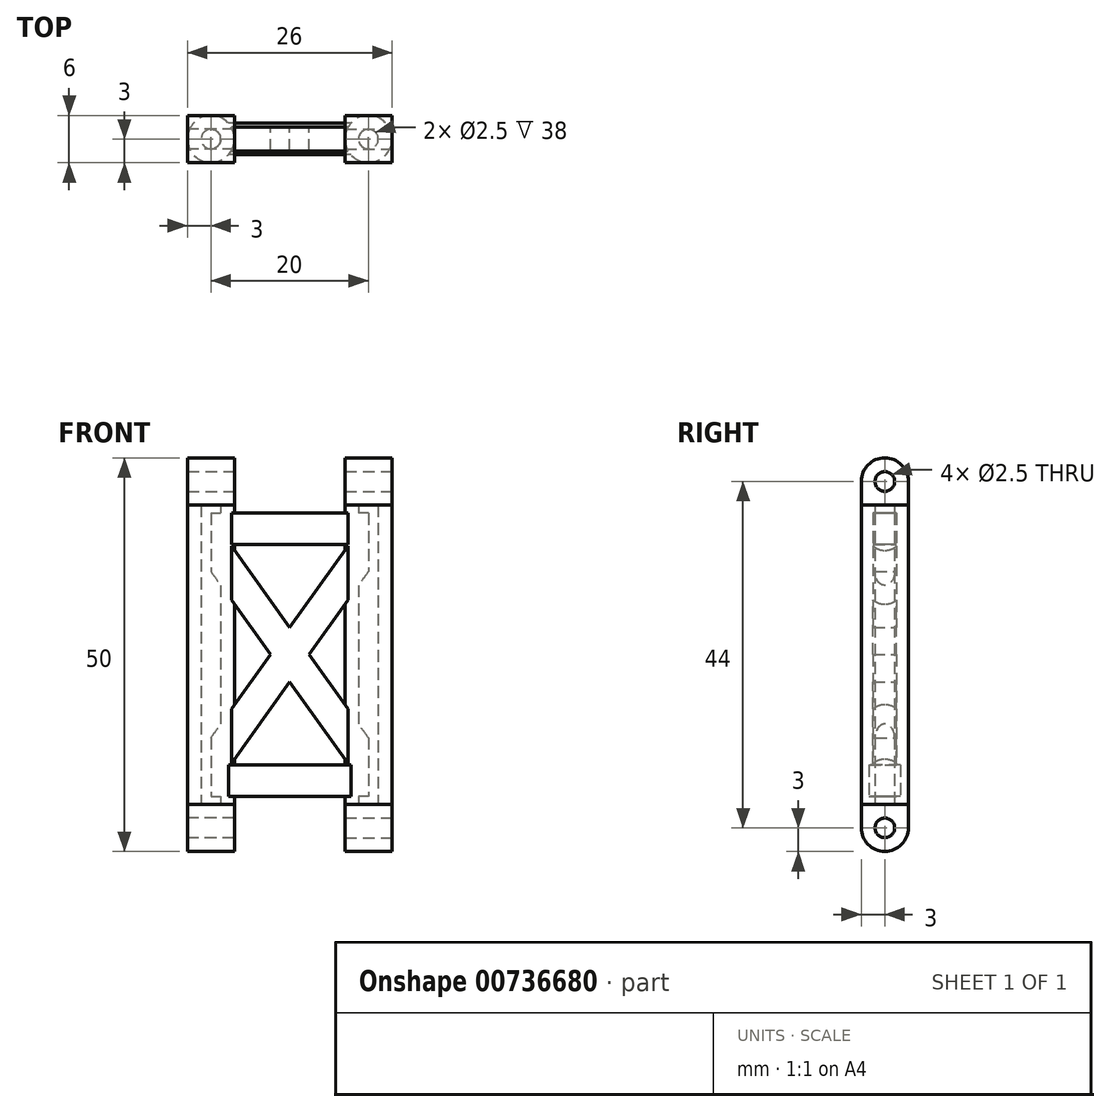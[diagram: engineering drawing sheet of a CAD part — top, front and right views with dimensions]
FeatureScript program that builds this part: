
annotation { "Feature Type Name" : "Feature", "Feature Type Description" : "" }
export const myFeature = defineFeature(function(context is Context, id is Id, definition is map)
    precondition{}
    {
        {
            var Q0;
            Q0=qCreatedBy(makeId("Top.planeOp"),FACE);
            var sketch = newSketch(context, id + "F0", { "sketchPlane" : qUnion([Q0])});
            skCircle(sketch, "E0", {"center": v(-10, 0) * mm, "radius": 3 * mm});
            skCircle(sketch, "E1", {"center": v(10, 0) * mm, "radius": 3 * mm});
            skCircle(sketch, "E2", {"center": v(-10, 0) * mm, "radius": 1.25 * mm});
            skCircle(sketch, "E3", {"center": v(10, 0) * mm, "radius": 1.25 * mm});
            skLineSegment(sketch, "E4.bottom", {"start": v(-13, 3) * mm, "end": v(-7, 3) * mm});
            skLineSegment(sketch, "E4.top", {"start": v(-13, -3) * mm, "end": v(-7, -3) * mm});
            skLineSegment(sketch, "E4.left", {"start": v(-13, 3) * mm, "end": v(-13, -3) * mm});
            skLineSegment(sketch, "E4.right", {"start": v(-7, 3) * mm, "end": v(-7, -3) * mm});
            skLineSegment(sketch, "E5.bottom", {"start": v(7, -3) * mm, "end": v(13, -3) * mm});
            skLineSegment(sketch, "E5.top", {"start": v(7, 3) * mm, "end": v(13, 3) * mm});
            skLineSegment(sketch, "E5.left", {"start": v(7, -3) * mm, "end": v(7, 3) * mm});
            skLineSegment(sketch, "E5.right", {"start": v(13, -3) * mm, "end": v(13, 3) * mm});
            skSolve(sketch);
        }
        {
            var Q0;
            Q0=makeQuery(id+"F0.imprint","IMPRINT",FACE,{"disambiguationData":[TD([[makeQuery(id+"F0.imprint","IMPRINT",EDGE,{"derivedFrom":sQuery(id+"F0.wireOp",EDGE,"E3")}),-1.0]])]});
            var Q1;
            {var subQ0=sQuery(id+"F0.wireOp",EDGE,"E5.top");var subQ1=sQuery(id+"F0.wireOp",EDGE,"E1");var subQ2=makeQuery(id+"F0.imprint","INTERSECT",VERTEX,{"derivedFrom":[subQ1,subQ0]});Q1=makeQuery(id+"F0.imprint","IMPRINT",FACE,{"disambiguationData":[TD([[makeQuery(id+"F0.imprint","IMPRINT",EDGE,{"disambiguationData":[TD([[subQ2,-1.0]])],"derivedFrom":subQ1}),-1.0]])]});}
            var Q2;
            {var subQ0=sQuery(id+"F0.wireOp",EDGE,"E5.left");var subQ1=sQuery(id+"F0.wireOp",EDGE,"E1");var subQ2=makeQuery(id+"F0.imprint","INTERSECT",VERTEX,{"derivedFrom":[subQ1,subQ0]});Q2=makeQuery(id+"F0.imprint","IMPRINT",FACE,{"disambiguationData":[TD([[makeQuery(id+"F0.imprint","IMPRINT",EDGE,{"disambiguationData":[TD([[subQ2,-1.0]])],"derivedFrom":subQ1}),-1.0]])]});}
            var Q3;
            {var subQ0=sQuery(id+"F0.wireOp",EDGE,"E5.right");var subQ1=sQuery(id+"F0.wireOp",EDGE,"E1");var subQ2=makeQuery(id+"F0.imprint","INTERSECT",VERTEX,{"derivedFrom":[subQ1,subQ0]});Q3=makeQuery(id+"F0.imprint","IMPRINT",FACE,{"disambiguationData":[TD([[makeQuery(id+"F0.imprint","IMPRINT",EDGE,{"disambiguationData":[TD([[subQ2,1.0]])],"derivedFrom":subQ1}),-1.0]])]});}
            var Q4;
            {var subQ0=sQuery(id+"F0.wireOp",EDGE,"E5.top");var subQ1=sQuery(id+"F0.wireOp",EDGE,"E1");var subQ2=makeQuery(id+"F0.imprint","INTERSECT",VERTEX,{"derivedFrom":[subQ1,subQ0]});Q4=makeQuery(id+"F0.imprint","IMPRINT",FACE,{"disambiguationData":[TD([[makeQuery(id+"F0.imprint","IMPRINT",EDGE,{"disambiguationData":[TD([[subQ2,1.0]])],"derivedFrom":subQ1}),-1.0]])]});}
            var Q5;
            {var subQ0=sQuery(id+"F0.wireOp",EDGE,"E4.bottom");var subQ1=sQuery(id+"F0.wireOp",EDGE,"E0");var subQ2=makeQuery(id+"F0.imprint","INTERSECT",VERTEX,{"derivedFrom":[subQ1,subQ0]});Q5=makeQuery(id+"F0.imprint","IMPRINT",FACE,{"disambiguationData":[TD([[makeQuery(id+"F0.imprint","IMPRINT",EDGE,{"disambiguationData":[TD([[subQ2,1.0]])],"derivedFrom":subQ1}),-1.0]])]});}
            var Q6;
            {var subQ0=sQuery(id+"F0.wireOp",EDGE,"E4.bottom");var subQ1=sQuery(id+"F0.wireOp",EDGE,"E0");var subQ2=makeQuery(id+"F0.imprint","INTERSECT",VERTEX,{"derivedFrom":[subQ1,subQ0]});Q6=makeQuery(id+"F0.imprint","IMPRINT",FACE,{"disambiguationData":[TD([[makeQuery(id+"F0.imprint","IMPRINT",EDGE,{"disambiguationData":[TD([[subQ2,-1.0]])],"derivedFrom":subQ1}),-1.0]])]});}
            var Q7;
            Q7=makeQuery(id+"F0.imprint","IMPRINT",FACE,{"disambiguationData":[TD([[makeQuery(id+"F0.imprint","IMPRINT",EDGE,{"derivedFrom":sQuery(id+"F0.wireOp",EDGE,"E2")}),-1.0]])]});
            var Q8;
            {var subQ0=sQuery(id+"F0.wireOp",EDGE,"E4.left");var subQ1=sQuery(id+"F0.wireOp",EDGE,"E0");var subQ2=makeQuery(id+"F0.imprint","INTERSECT",VERTEX,{"derivedFrom":[subQ1,subQ0]});Q8=makeQuery(id+"F0.imprint","IMPRINT",FACE,{"disambiguationData":[TD([[makeQuery(id+"F0.imprint","IMPRINT",EDGE,{"disambiguationData":[TD([[subQ2,-1.0]])],"derivedFrom":subQ1}),-1.0]])]});}
            var Q9;
            {var subQ0=sQuery(id+"F0.wireOp",EDGE,"E4.right");var subQ1=sQuery(id+"F0.wireOp",EDGE,"E0");var subQ2=makeQuery(id+"F0.imprint","INTERSECT",VERTEX,{"derivedFrom":[subQ1,subQ0]});Q9=makeQuery(id+"F0.imprint","IMPRINT",FACE,{"disambiguationData":[TD([[makeQuery(id+"F0.imprint","IMPRINT",EDGE,{"disambiguationData":[TD([[subQ2,1.0]])],"derivedFrom":subQ1}),-1.0]])]});}
            var Q10;
            Q10=makeQuery(id+"F0.imprint","IMPRINT",FACE,{"disambiguationData":[TD([[makeQuery(id+"F0.imprint","IMPRINT",EDGE,{"derivedFrom":sQuery(id+"F0.wireOp",EDGE,"E2")}),1.0]])]});
            var Q11;
            Q11=makeQuery(id+"F0.imprint","IMPRINT",FACE,{"disambiguationData":[TD([[makeQuery(id+"F0.imprint","IMPRINT",EDGE,{"derivedFrom":sQuery(id+"F0.wireOp",EDGE,"E3")}),1.0]])]});
            extrude(context, id + "F1", {"entities" : qUnion([Q0, Q1, Q2, Q3, Q4, Q5, Q6, Q7, Q8, Q9, Q10, Q11]), "depth" : 6 * mm, "offsetDistance" : 25 * mm});
        }
        {
            var Q0;
            Q0=makeQuery(id+"F0.imprint","IMPRINT",FACE,{"disambiguationData":[TD([[makeQuery(id+"F0.imprint","IMPRINT",EDGE,{"derivedFrom":sQuery(id+"F0.wireOp",EDGE,"E3")}),-1.0]])]});
            extrude(context, id + "F2", {"entities" : qUnion([Q0]), "operationType" : NewBodyOperationType.ADD, "depth" : 50 * mm, "offsetDistance" : 25 * mm});
        }
        {
            var Q0;
            Q0=makeQuery(id+"F0.imprint","IMPRINT",FACE,{"disambiguationData":[TD([[makeQuery(id+"F0.imprint","IMPRINT",EDGE,{"derivedFrom":sQuery(id+"F0.wireOp",EDGE,"E2")}),-1.0]])]});
            extrude(context, id + "F3", {"entities" : qUnion([Q0]), "operationType" : NewBodyOperationType.ADD, "depth" : 50 * mm, "offsetDistance" : 25 * mm});
        }
        {
            var Q0;
            Q0=makeQuery(id+"F1.opExtrude","SWEPT_FACE",FACE,{"disambiguationData":[OSD([sQuery(id+"F0.wireOp",EDGE,"E5.right")])]});
            var sketch = newSketch(context, id + "F4", { "sketchPlane" : qUnion([Q0])});
            skCircle(sketch, "E6", {"center": v(0, 3) * mm, "radius": 1.25 * mm});
            skPoint(sketch, "E6.centerSnap0", {"position": v(-3, 3) * mm});
            skCircle(sketch, "E7", {"center": v(0, 3) * mm, "radius": 3 * mm});
            skSolve(sketch);
        }
        {
            var Q0;
            Q0=makeQuery(id+"F4.imprint","IMPRINT",FACE,{"disambiguationData":[TD([[makeQuery(id+"F4.imprint","IMPRINT",EDGE,{"derivedFrom":sQuery(id+"F4.wireOp",EDGE,"E6")}),1.0]])]});
            var Q1;
            {var subQ0=sQuery(id+"F4.wireOp",EDGE,"E7");var subQ1=sQuery(id+"F0.wireOp",EDGE,"E5.right");var subQ4=makeQuery(id+"F1.opExtrude","CAP_EDGE",EDGE,{"disambiguationData":[OSD([subQ1])],"isStart":true});var subQ5=makeQuery(id+"F4.imprint","INTERSECT",VERTEX,{"derivedFrom":[subQ4,subQ0]});Q1=makeQuery(id+"F4.imprint","IMPRINT",FACE,{"disambiguationData":[TD([[makeQuery(id+"F4.imprint","IMPRINT",EDGE,{"disambiguationData":[TD([[subQ5,1.0]])],"derivedFrom":subQ0}),-1.0]])]});}
            var Q2;
            {var subQ0=sQuery(id+"F4.wireOp",EDGE,"E7");var subQ1=sQuery(id+"F0.wireOp",EDGE,"E5.right");var subQ4=makeQuery(id+"F1.opExtrude","CAP_EDGE",EDGE,{"disambiguationData":[OSD([subQ1])],"isStart":true});var subQ5=makeQuery(id+"F4.imprint","INTERSECT",VERTEX,{"derivedFrom":[subQ4,subQ0]});Q2=makeQuery(id+"F4.imprint","IMPRINT",FACE,{"disambiguationData":[TD([[makeQuery(id+"F4.imprint","IMPRINT",EDGE,{"disambiguationData":[TD([[subQ5,-1.0]])],"derivedFrom":subQ0}),-1.0]])]});}
            extrude(context, id + "F5", {"entities" : qUnion([Q0, Q1, Q2]), "operationType" : NewBodyOperationType.REMOVE, "oppositeDirection" : true, "depth" : 6 * mm, "offsetDistance" : 25 * mm});
        }
        {
            var Q0;
            Q0=makeQuery(id+"F1.opExtrude","SWEPT_FACE",FACE,{"disambiguationData":[OSD([sQuery(id+"F0.wireOp",EDGE,"E4.left")])]});
            var sketch = newSketch(context, id + "F6", { "sketchPlane" : qUnion([Q0])});
            skCircle(sketch, "E8", {"center": v(0, 3) * mm, "radius": 1.25 * mm});
            skPoint(sketch, "E8.centerSnap0", {"position": v(-3, 3) * mm});
            skCircle(sketch, "E9", {"center": v(0, 3) * mm, "radius": 3 * mm});
            skSolve(sketch);
        }
        {
            var Q0;
            Q0=makeQuery(id+"F6.imprint","IMPRINT",FACE,{"disambiguationData":[TD([[makeQuery(id+"F6.imprint","IMPRINT",EDGE,{"derivedFrom":sQuery(id+"F6.wireOp",EDGE,"E8")}),1.0]])]});
            var Q1;
            {var subQ0=sQuery(id+"F6.wireOp",EDGE,"E9");var subQ1=sQuery(id+"F0.wireOp",EDGE,"E4.left");var subQ4=makeQuery(id+"F1.opExtrude","CAP_EDGE",EDGE,{"disambiguationData":[OSD([subQ1])],"isStart":true});var subQ5=makeQuery(id+"F6.imprint","INTERSECT",VERTEX,{"derivedFrom":[subQ4,subQ0]});Q1=makeQuery(id+"F6.imprint","IMPRINT",FACE,{"disambiguationData":[TD([[makeQuery(id+"F6.imprint","IMPRINT",EDGE,{"disambiguationData":[TD([[subQ5,1.0]])],"derivedFrom":subQ0}),-1.0]])]});}
            var Q2;
            {var subQ0=sQuery(id+"F6.wireOp",EDGE,"E9");var subQ1=sQuery(id+"F0.wireOp",EDGE,"E4.left");var subQ4=makeQuery(id+"F1.opExtrude","CAP_EDGE",EDGE,{"disambiguationData":[OSD([subQ1])],"isStart":true});var subQ5=makeQuery(id+"F6.imprint","INTERSECT",VERTEX,{"derivedFrom":[subQ4,subQ0]});Q2=makeQuery(id+"F6.imprint","IMPRINT",FACE,{"disambiguationData":[TD([[makeQuery(id+"F6.imprint","IMPRINT",EDGE,{"disambiguationData":[TD([[subQ5,-1.0]])],"derivedFrom":subQ0}),-1.0]])]});}
            extrude(context, id + "F7", {"entities" : qUnion([Q0, Q1, Q2]), "operationType" : NewBodyOperationType.REMOVE, "oppositeDirection" : true, "depth" : 6 * mm, "offsetDistance" : 25 * mm});
        }
        {
            var Q0;
            Q0=qCreatedBy(makeId("Front.planeOp"),FACE);
            var sketch = newSketch(context, id + "F8", { "sketchPlane" : qUnion([Q0])});
            skLineSegment(sketch, "E10.bottom", {"start": v(10, 7) * mm, "end": v(-10, 7) * mm});
            skLineSegment(sketch, "E10.top", {"start": v(10, 11) * mm, "end": v(-10, 11) * mm});
            skLineSegment(sketch, "E10.left", {"start": v(10, 7) * mm, "end": v(10, 11) * mm});
            skLineSegment(sketch, "E10.right", {"start": v(-10, 7) * mm, "end": v(-10, 11) * mm});
            skLineSegment(sketch, "E11.bottom", {"start": v(-10, 43) * mm, "end": v(10, 43) * mm});
            skLineSegment(sketch, "E11.top", {"start": v(-10, 39) * mm, "end": v(10, 39) * mm});
            skLineSegment(sketch, "E11.left", {"start": v(-10, 43) * mm, "end": v(-10, 39) * mm});
            skLineSegment(sketch, "E11.right", {"start": v(10, 43) * mm, "end": v(10, 39) * mm});
            skLineSegment(sketch, "E12", {"start": v(-10, 39) * mm, "end": v(10, 11) * mm, "construction": true});
            skLineSegment(sketch, "E13", {"start": v(10, 39) * mm, "end": v(-10, 11) * mm, "construction": true});
            skLineSegment(sketch, "E14", {"start": v(-10, 39) * mm, "end": v(-10, 11) * mm});
            skLineSegment(sketch, "E15", {"start": v(10, 11) * mm, "end": v(10, 39) * mm});
            skLineSegment(sketch, "E16", {"start": v(-7.54, 11) * mm, "end": v(10, 35.56) * mm});
            skLineSegment(sketch, "E17", {"start": v(7.54, 39) * mm, "end": v(-10, 14.44) * mm});
            skLineSegment(sketch, "E18", {"start": v(-7.54, 39) * mm, "end": v(10, 14.44) * mm});
            skLineSegment(sketch, "E19", {"start": v(7.54, 11) * mm, "end": v(-10, 35.56) * mm});
            skSolve(sketch);
        }
        {
            var Q0;
            Q0=makeQuery(id+"F8.imprint","IMPRINT",FACE,{"disambiguationData":[TD([[makeQuery(id+"F8.imprint","IMPRINT",EDGE,{"derivedFrom":sQuery(id+"F8.wireOp",EDGE,"E10.bottom")}),-1.0]])]});
            extrude(context, id + "F9", {"entities" : qUnion([Q0]), "endBound" : BoundingType.SYMMETRIC, "depth" : 4 * mm, "offsetDistance" : 25 * mm});
        }
        {
            var Q0;
            Q0=makeQuery(id+"F3.opExtrude","CAP_FACE",FACE,{"disambiguationData":[OSD([sQuery(id+"F0.wireOp",EDGE,"E0"),sQuery(id+"F0.wireOp",EDGE,"E2")])],"isStart":false});
            var sketch = newSketch(context, id + "F10", { "sketchPlane" : qUnion([Q0])});
            skLineSegment(sketch, "E20.bottom", {"start": v(-13, 3) * mm, "end": v(-7, 3) * mm});
            skLineSegment(sketch, "E20.top", {"start": v(-13, -3) * mm, "end": v(-7, -3) * mm});
            skLineSegment(sketch, "E20.left", {"start": v(-13, 3) * mm, "end": v(-13, -3) * mm});
            skLineSegment(sketch, "E20.right", {"start": v(-7, 3) * mm, "end": v(-7, -3) * mm});
            skLineSegment(sketch, "E21.bottom", {"start": v(7, 3) * mm, "end": v(13, 3) * mm});
            skLineSegment(sketch, "E21.top", {"start": v(7, -3) * mm, "end": v(13, -3) * mm});
            skLineSegment(sketch, "E21.left", {"start": v(7, 3) * mm, "end": v(7, -3) * mm});
            skLineSegment(sketch, "E21.right", {"start": v(13, 3) * mm, "end": v(13, -3) * mm});
            skSolve(sketch);
        }
        {
            var Q0;
            {var subQ0=sQuery(id+"F8.wireOp",EDGE,"E18");var subQ3=sQuery(id+"F8.wireOp",EDGE,"E17");var subQ4=makeQuery(id+"F8.imprint","INTERSECT",VERTEX,{"derivedFrom":[subQ3,subQ0]});Q0=makeQuery(id+"F8.imprint","IMPRINT",FACE,{"disambiguationData":[TD([[makeQuery(id+"F8.imprint","IMPRINT",EDGE,{"disambiguationData":[TD([[subQ4,-1.0]])],"derivedFrom":subQ3}),-1.0]])]});}
            var Q1;
            {var subQ0=sQuery(id+"F8.wireOp",EDGE,"E19");var subQ1=sQuery(id+"F8.wireOp",EDGE,"E16");var subQ2=makeQuery(id+"F8.imprint","INTERSECT",VERTEX,{"derivedFrom":[subQ1,subQ0]});Q1=makeQuery(id+"F8.imprint","IMPRINT",FACE,{"disambiguationData":[TD([[makeQuery(id+"F8.imprint","IMPRINT",EDGE,{"disambiguationData":[TD([[subQ2,-1.0]])],"derivedFrom":subQ1}),1.0]])]});}
            var Q2;
            {var subQ0=sQuery(id+"F8.wireOp",EDGE,"E19");var subQ1=sQuery(id+"F8.wireOp",EDGE,"E16");var subQ2=makeQuery(id+"F8.imprint","INTERSECT",VERTEX,{"derivedFrom":[subQ1,subQ0]});Q2=makeQuery(id+"F8.imprint","IMPRINT",FACE,{"disambiguationData":[TD([[makeQuery(id+"F8.imprint","IMPRINT",EDGE,{"disambiguationData":[TD([[subQ2,-1.0]])],"derivedFrom":subQ1}),-1.0]])]});}
            var Q3;
            {var subQ1=sQuery(id+"F8.wireOp",EDGE,"E10.top");var subQ5=sQuery(id+"F8.wireOp",EDGE,"E16");var subQ6=makeQuery(id+"F8.imprint","INTERSECT",VERTEX,{"derivedFrom":[subQ1,subQ5]});Q3=makeQuery(id+"F8.imprint","IMPRINT",FACE,{"disambiguationData":[TD([[makeQuery(id+"F8.imprint","IMPRINT",EDGE,{"disambiguationData":[TD([[subQ6,-1.0]])],"derivedFrom":subQ5}),1.0]])]});}
            var Q4;
            {var subQ5=sQuery(id+"F8.wireOp",EDGE,"E16");var subQ6=sQuery(id+"F8.wireOp",EDGE,"E15");var subQ7=makeQuery(id+"F8.imprint","INTERSECT",VERTEX,{"derivedFrom":[subQ6,subQ5]});Q4=makeQuery(id+"F8.imprint","IMPRINT",FACE,{"disambiguationData":[TD([[makeQuery(id+"F8.imprint","IMPRINT",EDGE,{"disambiguationData":[TD([[subQ7,1.0]])],"derivedFrom":subQ5}),1.0]])]});}
            var Q5;
            Q5=makeQuery(id+"F8.imprint","IMPRINT",FACE,{"disambiguationData":[TD([[makeQuery(id+"F8.imprint","IMPRINT",EDGE,{"derivedFrom":sQuery(id+"F8.wireOp",EDGE,"E11.bottom")}),-1.0]])]});
            extrude(context, id + "F11", {"entities" : qUnion([Q0, Q1, Q2, Q3, Q4, Q5]), "operationType" : NewBodyOperationType.ADD, "endBound" : BoundingType.SYMMETRIC, "depth" : 3 * mm, "offsetDistance" : 25 * mm});
        }
        {
            var Q0;
            Q0 = qSketchRegion(id + "F10", true);
            extrude(context, id + "F12", {"entities" : qUnion([Q0]), "operationType" : NewBodyOperationType.ADD, "oppositeDirection" : true, "depth" : 6 * mm, "offsetDistance" : 25 * mm});
        }
        {
            var Q0;
            Q0=makeQuery(id+"F12.opExtrude","SWEPT_FACE",FACE,{"disambiguationData":[OSD([sQuery(id+"F10.wireOp",EDGE,"E21.right")])]});
            var sketch = newSketch(context, id + "F13", { "sketchPlane" : qUnion([Q0])});
            skCircle(sketch, "E22", {"center": v(0, 47) * mm, "radius": 1.25 * mm});
            skPoint(sketch, "E22.centerSnap0", {"position": v(-3, 47) * mm});
            skPoint(sketch, "E22.centerSnap1", {"position": v(0, 50) * mm});
            skCircle(sketch, "E23", {"center": v(0, 47) * mm, "radius": 3 * mm});
            skSolve(sketch);
        }
        {
            var Q0;
            Q0=makeQuery(id+"F13.imprint","IMPRINT",FACE,{"disambiguationData":[TD([[makeQuery(id+"F13.imprint","IMPRINT",EDGE,{"derivedFrom":sQuery(id+"F13.wireOp",EDGE,"E22")}),1.0]])]});
            var Q1;
            {var subQ0=sQuery(id+"F13.wireOp",EDGE,"E23");var subQ1=sQuery(id+"F10.wireOp",EDGE,"E21.right");var subQ2=makeQuery(id+"F12.opExtrude","CAP_EDGE",EDGE,{"disambiguationData":[OSD([subQ1])],"isStart":true});var subQ3=makeQuery(id+"F13.imprint","INTERSECT",VERTEX,{"derivedFrom":[subQ2,subQ0]});Q1=makeQuery(id+"F13.imprint","IMPRINT",FACE,{"disambiguationData":[TD([[makeQuery(id+"F13.imprint","IMPRINT",EDGE,{"disambiguationData":[TD([[subQ3,-1.0]])],"derivedFrom":subQ0}),-1.0]])]});}
            var Q2;
            {var subQ0=sQuery(id+"F13.wireOp",EDGE,"E23");var subQ1=sQuery(id+"F10.wireOp",EDGE,"E21.right");var subQ2=makeQuery(id+"F12.opExtrude","CAP_EDGE",EDGE,{"disambiguationData":[OSD([subQ1])],"isStart":true});var subQ3=makeQuery(id+"F13.imprint","INTERSECT",VERTEX,{"derivedFrom":[subQ2,subQ0]});Q2=makeQuery(id+"F13.imprint","IMPRINT",FACE,{"disambiguationData":[TD([[makeQuery(id+"F13.imprint","IMPRINT",EDGE,{"disambiguationData":[TD([[subQ3,1.0]])],"derivedFrom":subQ0}),-1.0]])]});}
            extrude(context, id + "F14", {"entities" : qUnion([Q0, Q1, Q2]), "operationType" : NewBodyOperationType.REMOVE, "oppositeDirection" : true, "depth" : 30 * mm, "offsetDistance" : 25 * mm});
        }
    });
